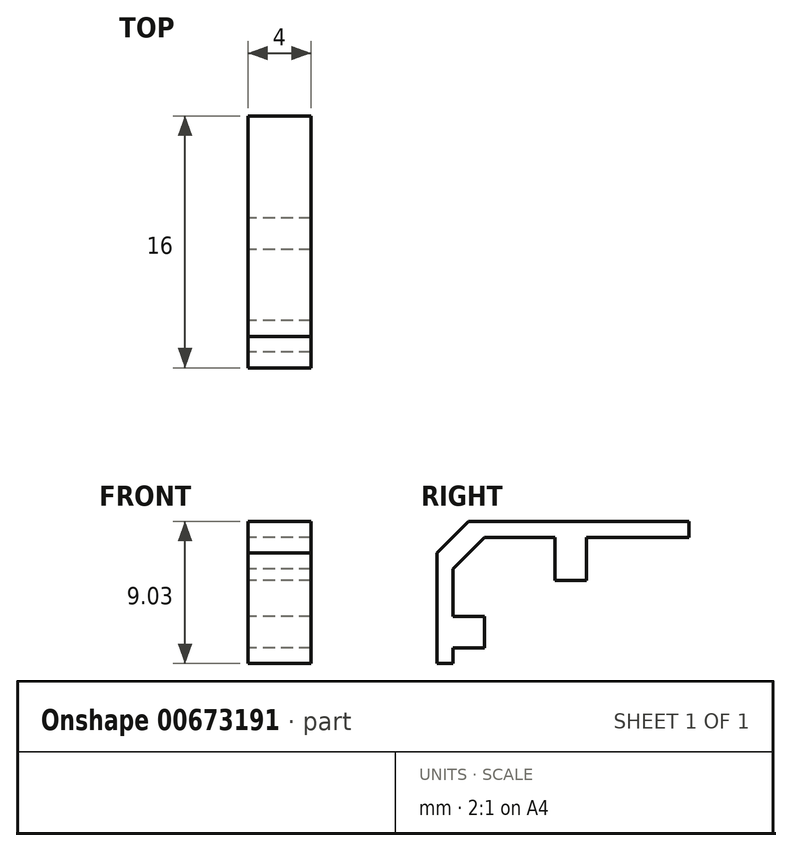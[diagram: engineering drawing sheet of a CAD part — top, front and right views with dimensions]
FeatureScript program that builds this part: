
annotation { "Feature Type Name" : "Feature", "Feature Type Description" : "" }
export const myFeature = defineFeature(function(context is Context, id is Id, definition is map)
    precondition{}
    {
        {
            var Q0;
            Q0=qCreatedBy(makeId("Right.planeOp"),FACE);
            var sketch = newSketch(context, id + "F0", { "sketchPlane" : qUnion([Q0])});
            skLineSegment(sketch, "E0.bottom", {"start": v(9.92, -6.58) * mm, "end": v(-5.08, -6.58) * mm});
            skLineSegment(sketch, "E0.top", {"start": v(9.92, 3.42) * mm, "end": v(3.42, 3.42) * mm});
            skLineSegment(sketch, "E0.left", {"start": v(9.92, -6.58) * mm, "end": v(9.92, 3.42) * mm});
            skLineSegment(sketch, "E0.right", {"start": v(-5.08, -6.58) * mm, "end": v(-5.08, -3.58) * mm});
            skLineSegment(sketch, "E1", {"start": v(-3.08, 3.42) * mm, "end": v(-5.08, 1.42) * mm});
            skPoint(sketch, "E2.orphan", {"position": v(-5.08, 3.42) * mm});
            skLineSegment(sketch, "E3", {"start": v(9.92, 4.45) * mm, "end": v(-5.08, 4.45) * mm, "construction": true});
            skLineSegment(sketch, "E4", {"start": v(1.42, 3.42) * mm, "end": v(1.42, 0.69) * mm});
            skLineSegment(sketch, "E5", {"start": v(1.42, 0.69) * mm, "end": v(3.42, 0.69) * mm});
            skLineSegment(sketch, "E6", {"start": v(3.42, 0.69) * mm, "end": v(3.42, 3.42) * mm});
            skLineSegment(sketch, "E7", {"start": v(-5.08, -3.58) * mm, "end": v(-3.08, -3.58) * mm});
            skLineSegment(sketch, "E8", {"start": v(-3.08, -3.58) * mm, "end": v(-3.08, -1.58) * mm});
            skLineSegment(sketch, "E9", {"start": v(-3.08, -1.58) * mm, "end": v(-5.08, -1.58) * mm});
            skLineSegment(sketch, "E10", {"start": v(-5.08, 3.42) * mm, "end": v(-6.08, 3.42) * mm, "construction": true});
            skLineSegment(sketch, "E11", {"start": v(-6.08, -4.58) * mm, "end": v(-5.08, -4.58) * mm});
            skLineSegment(sketch, "E12", {"start": v(-3.08, 3.42) * mm, "end": v(-3.08, 4.42) * mm, "construction": true});
            skLineSegment(sketch, "E13", {"start": v(-6.08, -4.58) * mm, "end": v(-6.08, 4.45) * mm});
            skLineSegment(sketch, "E14", {"start": v(-6.08, 4.45) * mm, "end": v(9.92, 4.45) * mm});
            skLineSegment(sketch, "E15", {"start": v(9.92, 3.42) * mm, "end": v(9.92, 4.45) * mm});
            skLineSegment(sketch, "E16.trimOffspring", {"start": v(-5.08, -1.58) * mm, "end": v(-5.08, 1.42) * mm});
            skLineSegment(sketch, "E17.trimOffspring", {"start": v(1.42, 3.42) * mm, "end": v(-3.08, 3.42) * mm});
            skSolve(sketch);
        }
        {
            var Q0;
            Q0=makeQuery(id+"F0.imprint","IMPRINT",FACE,{"disambiguationData":[TD([[makeQuery(id+"F0.imprint","IMPRINT",EDGE,{"derivedFrom":sQuery(id+"F0.wireOp",EDGE,"E0.top")}),-1.0]])]});
            extrude(context, id + "F1", {"entities" : qUnion([Q0]), "depth" : 4 * mm});
        }
        {
            var Q0;
            Q0=makeQuery(id+"F1.opExtrude","SWEPT_EDGE",EDGE,{"disambiguationData":[OSD([sQuery(id+"F0.wireOp",EDGE,"E13"),sQuery(id+"F0.wireOp",EDGE,"E14")])]});
            chamfer(context, id + "F2", {"entities" : qUnion([Q0]), "width" : 2 * mm, "tangentPropagation" : true});
        }
    });
